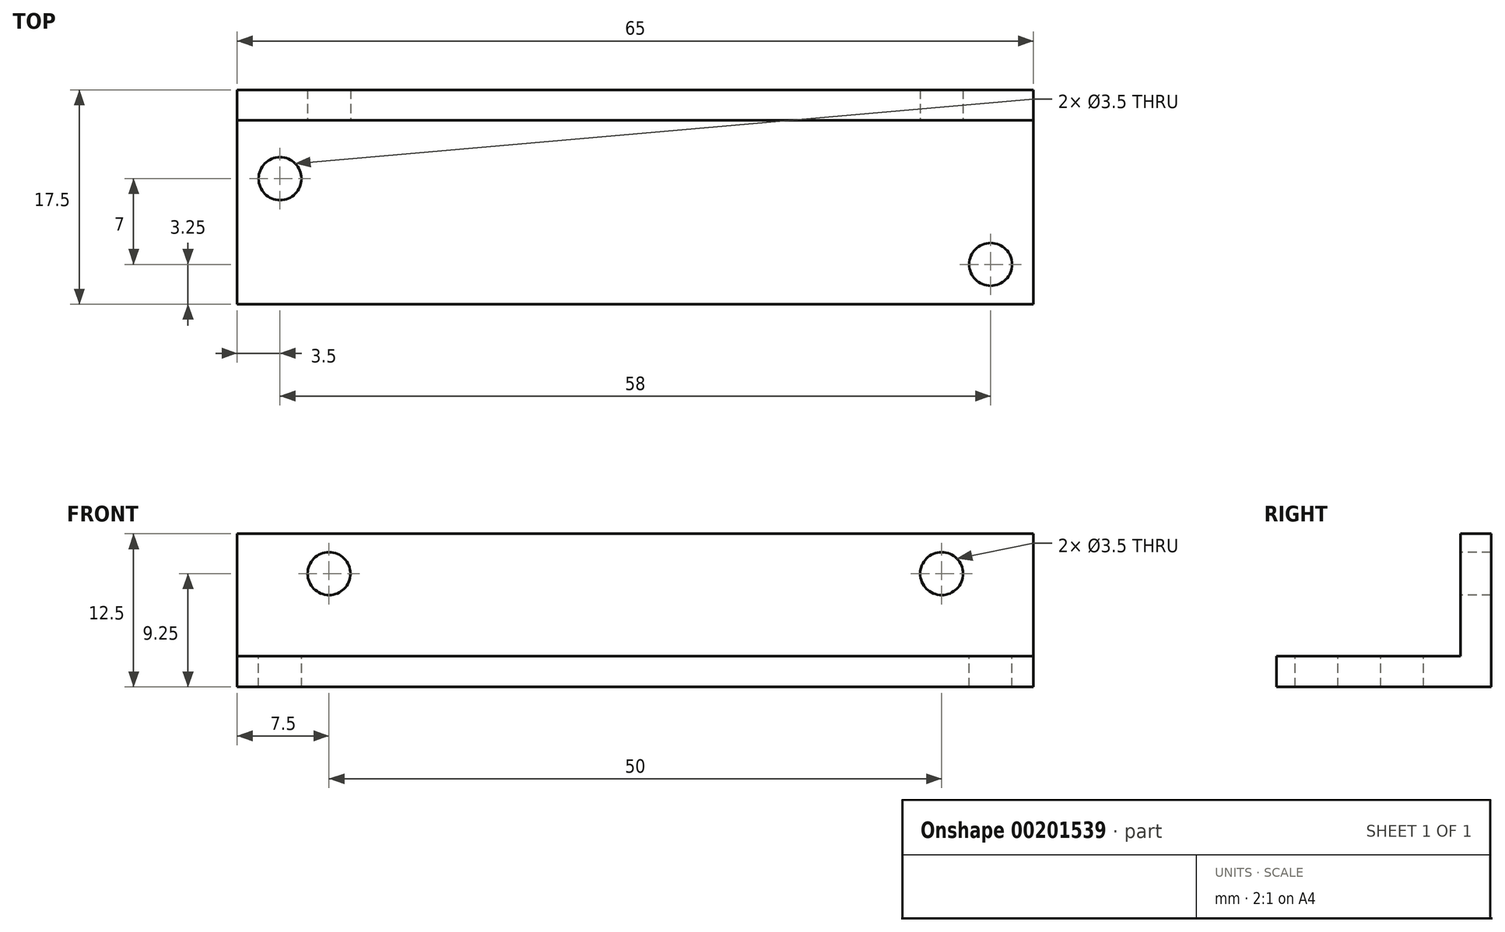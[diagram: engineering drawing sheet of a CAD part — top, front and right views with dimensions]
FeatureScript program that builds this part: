
annotation { "Feature Type Name" : "Feature", "Feature Type Description" : "" }
export const myFeature = defineFeature(function(context is Context, id is Id, definition is map)
    precondition{}
    {
        {
            var Q0;
            Q0=qCreatedBy(makeId("Right.planeOp"),FACE);
            var sketch = newSketch(context, id + "F0", { "sketchPlane" : qUnion([Q0])});
            skLineSegment(sketch, "E0", {"start": v(0, 0) * mm, "end": v(0, 12.5) * mm});
            skLineSegment(sketch, "E1", {"start": v(0, 12.5) * mm, "end": v(-2.5, 12.5) * mm});
            skLineSegment(sketch, "E2", {"start": v(-2.5, 12.5) * mm, "end": v(-2.5, 2.5) * mm});
            skLineSegment(sketch, "E3", {"start": v(-2.5, 2.5) * mm, "end": v(-17.5, 2.5) * mm});
            skLineSegment(sketch, "E4", {"start": v(-17.5, 2.5) * mm, "end": v(-17.5, 0) * mm});
            skLineSegment(sketch, "E5", {"start": v(-17.5, 0) * mm, "end": v(0, 0) * mm});
            skSolve(sketch);
        }
        {
            var Q0;
            Q0=makeQuery(id+"F0.imprint","IMPRINT",FACE,{"disambiguationData":[TD([[makeQuery(id+"F0.imprint","IMPRINT",EDGE,{"derivedFrom":sQuery(id+"F0.wireOp",EDGE,"E0")}),1.0]])]});
            extrude(context, id + "F1", {"entities" : qUnion([Q0]), "depth" : 65 * mm});
        }
        {
            var Q0;
            Q0=makeQuery(id+"F1.opExtrude","SWEPT_FACE",FACE,{"disambiguationData":[OSD([sQuery(id+"F0.wireOp",EDGE,"E2")])]});
            var sketch = newSketch(context, id + "F2", { "sketchPlane" : qUnion([Q0])});
            skCircle(sketch, "E6", {"center": v(7.5, 9.25) * mm, "radius": 1.75 * mm});
            skLineSegment(sketch, "E7", {"start": v(32.5, 12.5) * mm, "end": v(32.5, 2.5) * mm, "construction": true});
            skCircle(sketch, "E8.MirrorC", {"center": v(57.5, 9.25) * mm, "radius": 1.75 * mm});
            skSolve(sketch);
        }
        {
            var Q0;
            Q0 = qSketchRegion(id + "F2", true);
            extrude(context, id + "F3", {"entities" : qUnion([Q0]), "operationType" : NewBodyOperationType.REMOVE, "endBound" : BoundingType.THROUGH_ALL, "oppositeDirection" : true, "depth" : 25 * mm});
        }
        {
            var Q0;
            Q0=makeQuery(id+"F1.opExtrude","SWEPT_FACE",FACE,{"disambiguationData":[OSD([sQuery(id+"F0.wireOp",EDGE,"E3")])]});
            var sketch = newSketch(context, id + "F4", { "sketchPlane" : qUnion([Q0])});
            skCircle(sketch, "E9", {"center": v(3.5, -7.25) * mm, "radius": 1.75 * mm});
            skCircle(sketch, "E10", {"center": v(61.5, -14.25) * mm, "radius": 1.75 * mm});
            skLineSegment(sketch, "E11", {"start": v(61.5, -14.25) * mm, "end": v(65, -14.25) * mm, "construction": true});
            skLineSegment(sketch, "E12", {"start": v(3.5, -7.25) * mm, "end": v(0, -7.25) * mm, "construction": true});
            skSolve(sketch);
        }
        {
            var Q0;
            Q0 = qSketchRegion(id + "F4", true);
            extrude(context, id + "F5", {"entities" : qUnion([Q0]), "operationType" : NewBodyOperationType.REMOVE, "endBound" : BoundingType.THROUGH_ALL, "oppositeDirection" : true, "depth" : 25 * mm});
        }
    });
